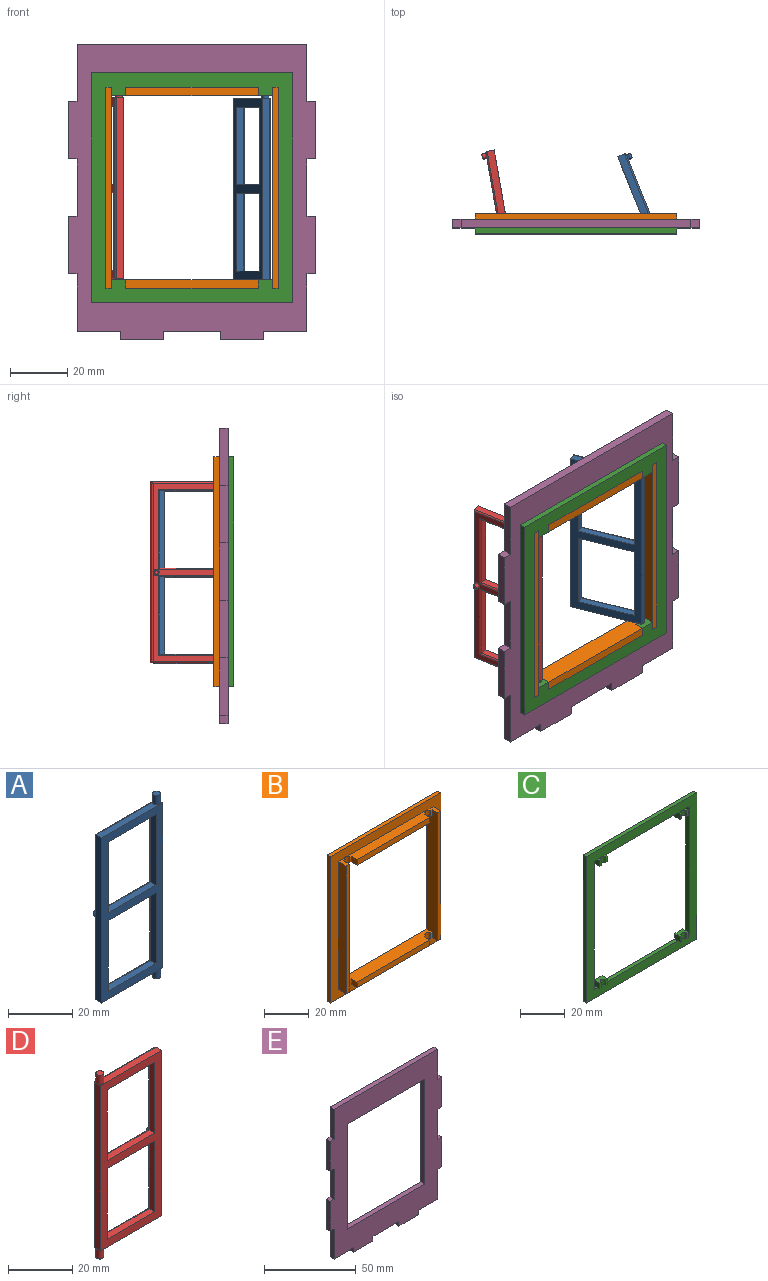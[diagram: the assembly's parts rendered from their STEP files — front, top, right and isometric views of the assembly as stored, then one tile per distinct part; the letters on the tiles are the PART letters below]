
ASSEMBLY  parts=5 mates=10
PART A: 38 faces, bbox 27x4.5x70 mm
  f0: plane 1x0.5mm, normal (0,0,-1), area 0.2mm2, adj f13,f18,f20
  f1: plane 27x2.5mm, normal (0,0,1), area 62.7mm2, adj f3,f13,f14,f17,f27
  f2: plane 27x2.5mm, normal (0,0,-1), area 62.7mm2, adj f3,f13,f14,f18,f23
  f3: plane 63x2.5mm, normal (-1,0,0), area 157.5mm2, adj f1,f2,f14,f25
  f4: plane 1x0.5mm, normal (0,0,1), area 0.2mm2, adj f13,f17,f24
  f5: plane 27x2.5mm, normal (1,0,0), area 67.5mm2, adj f6,f11,f14,f29
  f6: plane 21x2.5mm, normal (0,0,1), area 52.5mm2, adj f5,f7,f14,f28
  f7: plane 27x2.5mm, normal (-1,0,0), area 67.5mm2, adj f6,f11,f14,f30
  f8: plane 21x2.5mm, normal (0,0,-1), area 52.5mm2, adj f9,f12,f14,f33
  f9: plane 27x2.5mm, normal (1,0,0), area 67.5mm2, adj f8,f10,f14,f32
  f10: plane 21x2.5mm, normal (0,0,1), area 52.5mm2, adj f9,f12,f14,f34
  f11: plane 21x2.5mm, normal (0,0,-1), area 52.5mm2, adj f5,f7,f14,f31
  f12: plane 27x2.5mm, normal (-1,0,0), area 67.5mm2, adj f8,f10,f14,f35
  f13: plane 63x2.5mm, normal (1,0,0), area 157.5mm2, adj f0,f1,f2,f4,f14,f22
  f14: plane 63x27mm, normal (0,-1,0), area 567mm2, adj f1,f2,f3,f5,f6,f7,f8,f9
  f15: plane 62.14x26mm, normal (0,1,0), area 377mm2, adj f21,f22,f23,f25,f26,f27,f28,f29
  f16: plane 2.5x2.5mm, normal (0,0,1), area 4.9mm2, adj f17
  f17: cylinder r=1.25mm len=3.5mm, axis (0,0,-1), area 27.5mm2, adj f1,f4,f16,f26
  f18: cylinder r=1.25mm len=3.5mm, axis (0,0,-1), area 27.5mm2, adj f0,f2,f19,f21
  f19: plane 2.5x2.5mm, normal (0,0,-1), area 4.9mm2, adj f18
  f20: cylinder r=0.5mm len=0.5mm, axis (-1,0,0), area 0.2mm2, adj f0,f21,f22
  f21: bspline ~1.88x0.61mm, area 0.9mm2, adj f15,f18,f20,f23
  f22: cylinder r=0.5mm len=63mm, axis (0,0,-1), area 49.1mm2, adj f13,f15,f20,f24
  f23: cylinder r=0.5mm len=25mm, axis (-1,0,0), area 19.4mm2, adj f2,f15,f21,f25
  f24: cylinder r=0.5mm len=0.5mm, axis (1,0,0), area 0.2mm2, adj f4,f22,f26
  f25: cylinder r=0.5mm len=63mm, axis (0,0,1), area 49.1mm2, adj f3,f15,f23,f27
  f26: bspline ~1.88x0.61mm, area 0.9mm2, adj f15,f17,f24,f27
  f27: cylinder r=0.5mm len=25mm, axis (1,0,0), area 19.4mm2, adj f1,f15,f25,f26
  f28: cylinder r=0.5mm len=22mm, axis (1,0,0), area 16.9mm2, adj f6,f15,f29,f30
  f29: cylinder r=0.5mm len=28mm, axis (0,0,-1), area 21.6mm2, adj f5,f15,f28,f31
  f30: cylinder r=0.5mm len=28mm, axis (0,0,1), area 21.6mm2, adj f7,f15,f28,f31
  f31: cylinder r=0.5mm len=22mm, axis (-1,0,0), area 16.9mm2, adj f11,f15,f29,f30
  f32: cylinder r=0.5mm len=28mm, axis (0,0,-1), area 21.6mm2, adj f9,f15,f33,f34
  f33: cylinder r=0.5mm len=22mm, axis (-1,0,0), area 16.9mm2, adj f8,f15,f32,f35
  f34: cylinder r=0.5mm len=22mm, axis (1,0,0), area 16.9mm2, adj f10,f15,f32,f35
  f35: cylinder r=0.5mm len=28mm, axis (0,0,1), area 21.6mm2, adj f12,f15,f33,f34
  f36: revolved ~2x2mm, area 9.3mm2, adj f15,f37
  f37: plane 1.34x1.34mm, normal (0,1,0), area 1.4mm2, adj f36
PART B: 38 faces, bbox 70x7x80 mm
  f0: plane 56x7mm, normal (0,0,-1), area 349.9mm2, adj f10,f12,f17,f18,f30,f31,f32,f33
  f1: plane 56x7mm, normal (0,0,1), area 349.9mm2, adj f9,f12,f17,f18,f22,f23,f24,f25
  f2: plane 5x4.5mm, normal (0,0,1), area 12mm2, adj f8,f11,f17,f20,f34,f37
  f3: plane 51x5mm, normal (0,0,1), area 234mm2, adj f10,f11,f31,f32,f33,f35,f36,f37
  f4: plane 5x4.5mm, normal (0,0,1), area 12mm2, adj f11,f12,f19,f21,f30,f31
  f5: plane 5x4.5mm, normal (0,0,-1), area 12mm2, adj f8,f11,f17,f20,f26,f29
  f6: plane 5x4.5mm, normal (0,0,-1), area 12mm2, adj f11,f12,f19,f21,f24,f25
  f7: plane 51x5mm, normal (0,0,-1), area 234mm2, adj f9,f11,f22,f23,f24,f26,f27,f28
  f8: plane 70x2mm, normal (0,-1,0), area 140mm2, adj f2,f5,f17,f20
  f9: plane 46x3mm, normal (0,-1,0), area 138mm2, adj f1,f7,f22,f28
  f10: plane 46x3mm, normal (0,-1,0), area 138mm2, adj f0,f3,f33,f35
  f11: plane 80x70mm, normal (0,-1,0), area 1400mm2, adj f2,f3,f4,f5,f6,f7,f13,f14
  f12: plane 70x7mm, normal (-1,0,0), area 469mm2, adj f0,f1,f4,f6,f18,f21,f25,f30
  f13: plane 80x2mm, normal (1,0,0), area 160mm2, adj f11,f14,f16,f18
  f14: plane 70x2mm, normal (0,0,1), area 140mm2, adj f11,f13,f15,f18
  f15: plane 80x2mm, normal (-1,0,0), area 160mm2, adj f11,f14,f16,f18
  f16: plane 70x2mm, normal (0,0,-1), area 140mm2, adj f11,f13,f15,f18
  f17: plane 70x7mm, normal (1,0,0), area 469mm2, adj f0,f1,f2,f5,f8,f18,f29,f34
  f18: plane 80x70mm, normal (0,1,0), area 2016mm2, adj f0,f1,f12,f13,f14,f15,f16,f17
  f19: plane 70x5mm, normal (1,0,0), area 350mm2, adj f4,f6,f11,f21
  f20: plane 70x5mm, normal (-1,0,0), area 350mm2, adj f2,f5,f8,f11
  f21: plane 70x2mm, normal (0,-1,0), area 140mm2, adj f4,f6,f12,f19
  f22: plane 3.5x3mm, normal (1,0,0), area 10.5mm2, adj f1,f7,f9,f23
  f23: plane 3x1mm, normal (0,-1,0), area 3mm2, adj f1,f7,f22,f24
  f24: cylinder r=1.5mm len=3mm, axis (0,0,1), area 14.1mm2, adj f1,f6,f7,f23,f25
  f25: plane 3x1mm, normal (0,-1,0), area 3mm2, adj f1,f6,f12,f24
  f26: cylinder r=1.5mm len=3mm, axis (0,0,1), area 14.1mm2, adj f1,f5,f7,f27,f29
  f27: plane 3x1mm, normal (0,-1,0), area 3mm2, adj f1,f7,f26,f28
  f28: plane 3.5x3mm, normal (-1,0,0), area 10.5mm2, adj f1,f7,f9,f27
  f29: plane 3x1mm, normal (0,-1,0), area 3mm2, adj f1,f5,f17,f26
  f30: plane 3x1mm, normal (0,-1,0), area 3mm2, adj f0,f4,f12,f31
  f31: cylinder r=1.5mm len=3mm, axis (0,0,1), area 14.1mm2, adj f0,f3,f4,f30,f32
  f32: plane 3x1mm, normal (0,-1,0), area 3mm2, adj f0,f3,f31,f33
  f33: plane 3.5x3mm, normal (1,0,0), area 10.5mm2, adj f0,f3,f10,f32
  f34: plane 3x1mm, normal (0,-1,0), area 3mm2, adj f0,f2,f17,f37
  f35: plane 3.5x3mm, normal (-1,0,0), area 10.5mm2, adj f0,f3,f10,f36
  f36: plane 3x1mm, normal (0,-1,0), area 3mm2, adj f0,f3,f35,f37
  f37: cylinder r=1.5mm len=3mm, axis (0,0,1), area 14.1mm2, adj f0,f2,f3,f34,f36
PART C: 46 faces, bbox 70x3.5x80 mm
  f0: plane 5x3.5mm, normal (0,0,-1), area 14mm2, adj f4,f34,f35,f36,f37,f38
  f1: plane 5x3.5mm, normal (0,0,-1), area 14mm2, adj f4,f39,f40,f41,f42,f43
  f2: plane 5x3.5mm, normal (0,0,1), area 14mm2, adj f4,f18,f20,f26,f27,f28
  f3: plane 5x3.5mm, normal (0,0,1), area 14mm2, adj f4,f19,f21,f29,f30,f31
  f4: plane 80x70mm, normal (0,1,0), area 1460mm2, adj f0,f1,f2,f3,f12,f13,f14,f15
  f5: plane 2.5x1.5mm, normal (0,0,1), area 2mm2, adj f11,f34,f35,f36
  f6: plane 2.5x1.5mm, normal (0,0,1), area 2mm2, adj f11,f39,f40,f41
  f7: plane 2.5x1.5mm, normal (0,0,1), area 2mm2, adj f11,f41,f42,f43
  f8: plane 2.5x1.5mm, normal (0,0,-1), area 2mm2, adj f11,f20,f27,f28
  f9: plane 2.5x1.5mm, normal (0,0,-1), area 2mm2, adj f11,f18,f26,f27
  f10: plane 2.5x1.5mm, normal (0,0,-1), area 2mm2, adj f11,f19,f30,f31
  f11: plane 80x70mm, normal (0,-1,0), area 1400mm2, adj f5,f6,f7,f8,f9,f10,f12,f13
  f12: plane 80x2mm, normal (1,0,0), area 160mm2, adj f4,f11,f13,f15
  f13: plane 70x2mm, normal (0,0,1), area 140mm2, adj f4,f11,f12,f14
  f14: plane 80x2mm, normal (-1,0,0), area 160mm2, adj f4,f11,f13,f15
  f15: plane 70x2mm, normal (0,0,-1), area 140mm2, adj f4,f11,f12,f14
  f16: plane 2.5x1.5mm, normal (0,0,1), area 2mm2, adj f11,f36,f37,f38
  f17: plane 2.5x1.5mm, normal (0,0,-1), area 2mm2, adj f11,f21,f29,f30
  f18: plane 3.5x3mm, normal (1,0,0), area 10.5mm2, adj f2,f4,f9,f23,f26
  f19: plane 3.5x3mm, normal (-1,0,0), area 10.5mm2, adj f3,f4,f10,f31,f44
  f20: plane 3.5x3mm, normal (-1,0,0), area 10.5mm2, adj f2,f4,f8,f22,f28
  f21: plane 3.5x3mm, normal (1,0,0), area 10.5mm2, adj f3,f4,f17,f22,f29
  f22: plane 46x2mm, normal (0,0,1), area 92mm2, adj f4,f11,f20,f21
  f23: plane 2x2mm, normal (0,0,1), area 4mm2, adj f4,f11,f18,f33
  f24: plane 46x2mm, normal (0,0,-1), area 92mm2, adj f4,f11,f38,f39
  f25: plane 2x2mm, normal (0,0,-1), area 4mm2, adj f4,f11,f33,f34
  f26: plane 3x1mm, normal (0,-1,0), area 3mm2, adj f2,f9,f18,f27
  f27: cylinder r=1.5mm len=3mm, axis (0,0,1), area 14.1mm2, adj f2,f8,f9,f26,f28
  f28: plane 3x1mm, normal (0,-1,0), area 3mm2, adj f2,f8,f20,f27
  f29: plane 3x1mm, normal (0,-1,0), area 3mm2, adj f3,f17,f21,f30
  f30: cylinder r=1.5mm len=3mm, axis (0,0,1), area 14.1mm2, adj f3,f10,f17,f29,f31
  f31: plane 3x1mm, normal (0,-1,0), area 3mm2, adj f3,f10,f19,f30
  f32: plane 70x2mm, normal (1,0,0), area 140mm2, adj f4,f11,f44,f45
  f33: plane 70x2mm, normal (-1,0,0), area 140mm2, adj f4,f11,f23,f25
  f34: plane 3.5x3mm, normal (1,0,0), area 10.5mm2, adj f0,f4,f5,f25,f35
  f35: plane 3x1mm, normal (0,-1,0), area 3mm2, adj f0,f5,f34,f36
  f36: cylinder r=1.5mm len=3mm, axis (0,0,1), area 14.1mm2, adj f0,f5,f16,f35,f37
  f37: plane 3x1mm, normal (0,-1,0), area 3mm2, adj f0,f16,f36,f38
  f38: plane 3.5x3mm, normal (-1,0,0), area 10.5mm2, adj f0,f4,f16,f24,f37
  f39: plane 3.5x3mm, normal (1,0,0), area 10.5mm2, adj f1,f4,f6,f24,f40
  f40: plane 3x1mm, normal (0,-1,0), area 3mm2, adj f1,f6,f39,f41
  f41: cylinder r=1.5mm len=3mm, axis (0,0,1), area 14.1mm2, adj f1,f6,f7,f40,f42
  f42: plane 3x1mm, normal (0,-1,0), area 3mm2, adj f1,f7,f41,f43
  f43: plane 3.5x3mm, normal (-1,0,0), area 10.5mm2, adj f1,f4,f7,f42,f45
  f44: plane 2x2mm, normal (0,0,1), area 4mm2, adj f4,f11,f19,f32
  f45: plane 2x2mm, normal (0,0,-1), area 4mm2, adj f4,f11,f32,f43
PART D: 38 faces, bbox 27x4.5x70 mm
  f0: plane 1x0.5mm, normal (0,0,-1), area 0.2mm2, adj f13,f18,f20
  f1: plane 27x2.5mm, normal (0,0,1), area 62.7mm2, adj f3,f13,f14,f17,f27
  f2: plane 27x2.5mm, normal (0,0,-1), area 62.7mm2, adj f3,f13,f14,f18,f23
  f3: plane 63x2.5mm, normal (1,0,0), area 157.5mm2, adj f1,f2,f14,f25
  f4: plane 1x0.5mm, normal (0,0,1), area 0.2mm2, adj f13,f17,f24
  f5: plane 27x2.5mm, normal (-1,0,0), area 67.5mm2, adj f6,f11,f14,f29
  f6: plane 21x2.5mm, normal (0,0,1), area 52.5mm2, adj f5,f7,f14,f28
  f7: plane 27x2.5mm, normal (1,0,0), area 67.5mm2, adj f6,f11,f14,f30
  f8: plane 21x2.5mm, normal (0,0,-1), area 52.5mm2, adj f9,f12,f14,f33
  f9: plane 27x2.5mm, normal (-1,0,0), area 67.5mm2, adj f8,f10,f14,f32
  f10: plane 21x2.5mm, normal (0,0,1), area 52.5mm2, adj f9,f12,f14,f34
  f11: plane 21x2.5mm, normal (0,0,-1), area 52.5mm2, adj f5,f7,f14,f31
  f12: plane 27x2.5mm, normal (1,0,0), area 67.5mm2, adj f8,f10,f14,f35
  f13: plane 63x2.5mm, normal (-1,0,0), area 157.5mm2, adj f0,f1,f2,f4,f14,f22
  f14: plane 63x27mm, normal (0,-1,0), area 567mm2, adj f1,f2,f3,f5,f6,f7,f8,f9
  f15: plane 62.14x26mm, normal (0,1,0), area 377mm2, adj f21,f22,f23,f25,f26,f27,f28,f29
  f16: plane 2.5x2.5mm, normal (0,0,1), area 4.9mm2, adj f17
  f17: cylinder r=1.25mm len=3.5mm, axis (0,0,-1), area 27.5mm2, adj f1,f4,f16,f26
  f18: cylinder r=1.25mm len=3.5mm, axis (0,0,-1), area 27.5mm2, adj f0,f2,f19,f21
  f19: plane 2.5x2.5mm, normal (0,0,-1), area 4.9mm2, adj f18
  f20: cylinder r=0.5mm len=0.5mm, axis (1,0,0), area 0.2mm2, adj f0,f21,f22
  f21: bspline ~1.88x0.61mm, area 0.9mm2, adj f15,f18,f20,f23
  f22: cylinder r=0.5mm len=63mm, axis (0,0,-1), area 49.1mm2, adj f13,f15,f20,f24
  f23: cylinder r=0.5mm len=25mm, axis (1,0,0), area 19.4mm2, adj f2,f15,f21,f25
  f24: cylinder r=0.5mm len=0.5mm, axis (-1,0,0), area 0.2mm2, adj f4,f22,f26
  f25: cylinder r=0.5mm len=63mm, axis (0,0,1), area 49.1mm2, adj f3,f15,f23,f27
  f26: bspline ~1.88x0.61mm, area 0.9mm2, adj f15,f17,f24,f27
  f27: cylinder r=0.5mm len=25mm, axis (-1,0,0), area 19.4mm2, adj f1,f15,f25,f26
  f28: cylinder r=0.5mm len=22mm, axis (-1,0,0), area 16.9mm2, adj f6,f15,f29,f30
  f29: cylinder r=0.5mm len=28mm, axis (0,0,-1), area 21.6mm2, adj f5,f15,f28,f31
  f30: cylinder r=0.5mm len=28mm, axis (0,0,1), area 21.6mm2, adj f7,f15,f28,f31
  f31: cylinder r=0.5mm len=22mm, axis (1,0,0), area 16.9mm2, adj f11,f15,f29,f30
  f32: cylinder r=0.5mm len=28mm, axis (0,0,-1), area 21.6mm2, adj f9,f15,f33,f34
  f33: cylinder r=0.5mm len=22mm, axis (1,0,0), area 16.9mm2, adj f8,f15,f32,f35
  f34: cylinder r=0.5mm len=22mm, axis (-1,0,0), area 16.9mm2, adj f10,f15,f32,f35
  f35: cylinder r=0.5mm len=28mm, axis (0,0,1), area 21.6mm2, adj f12,f15,f33,f34
  f36: revolved ~2x2mm, area 9.3mm2, adj f15,f37
  f37: plane 1.34x1.34mm, normal (0,1,0), area 1.4mm2, adj f36
PART E: 34 faces, bbox 86x3x103 mm
  f0: plane 70x3mm, normal (-1,0,0), area 210mm2, adj f1,f31,f32,f33
  f1: plane 60x3mm, normal (0,0,1), area 180mm2, adj f0,f2,f32,f33
  f2: plane 70x3mm, normal (1,0,0), area 210mm2, adj f1,f31,f32,f33
  f3: plane 15x3mm, normal (0,0,-1), area 45mm2, adj f4,f30,f32,f33
  f4: plane 3x3mm, normal (-1,0,0), area 9mm2, adj f3,f5,f32,f33
  f5: plane 15x3mm, normal (0,0,-1), area 45mm2, adj f4,f6,f32,f33
  f6: plane 3x3mm, normal (1,0,0), area 9mm2, adj f5,f7,f32,f33
  f7: plane 20x3mm, normal (0,0,-1), area 60mm2, adj f6,f8,f32,f33
  f8: plane 3x3mm, normal (-1,0,0), area 9mm2, adj f7,f9,f32,f33
  f9: plane 15x3mm, normal (0,0,-1), area 45mm2, adj f8,f10,f32,f33
  f10: plane 3x3mm, normal (1,0,0), area 9mm2, adj f9,f11,f32,f33
  f11: plane 15x3mm, normal (0,0,-1), area 45mm2, adj f10,f12,f32,f33
  f12: plane 20x3mm, normal (1,0,0), area 60mm2, adj f11,f13,f32,f33
  f13: plane 3x3mm, normal (0,0,-1), area 9mm2, adj f12,f14,f32,f33
  f14: plane 20x3mm, normal (1,0,0), area 60mm2, adj f13,f15,f32,f33
  f15: plane 3x3mm, normal (0,0,1), area 9mm2, adj f14,f16,f32,f33
  f16: plane 20x3mm, normal (1,0,0), area 60mm2, adj f15,f17,f32,f33
  f17: plane 3x3mm, normal (0,0,-1), area 9mm2, adj f16,f18,f32,f33
  f18: plane 20x3mm, normal (1,0,0), area 60mm2, adj f17,f19,f32,f33
  f19: plane 3x3mm, normal (0,0,1), area 9mm2, adj f18,f20,f32,f33
  f20: plane 20x3mm, normal (1,0,0), area 60mm2, adj f19,f21,f32,f33
  f21: plane 80x3mm, normal (0,0,1), area 240mm2, adj f20,f22,f32,f33
  f22: plane 20x3mm, normal (-1,0,0), area 60mm2, adj f21,f23,f32,f33
  f23: plane 3x3mm, normal (0,0,1), area 9mm2, adj f22,f24,f32,f33
  f24: plane 20x3mm, normal (-1,0,0), area 60mm2, adj f23,f25,f32,f33
  f25: plane 3x3mm, normal (0,0,-1), area 9mm2, adj f24,f26,f32,f33
  f26: plane 20x3mm, normal (-1,0,0), area 60mm2, adj f25,f27,f32,f33
  f27: plane 3x3mm, normal (0,0,1), area 9mm2, adj f26,f28,f32,f33
  f28: plane 20x3mm, normal (-1,0,0), area 60mm2, adj f27,f29,f32,f33
  f29: plane 3x3mm, normal (0,0,-1), area 9mm2, adj f28,f30,f32,f33
  f30: plane 20x3mm, normal (-1,0,0), area 60mm2, adj f3,f29,f32,f33
  f31: plane 60x3mm, normal (0,0,-1), area 180mm2, adj f0,f2,f32,f33
  f32: plane 103x86mm, normal (0,-1,0), area 4130mm2, adj f0,f1,f2,f3,f4,f5,f6,f7
  f33: plane 103x86mm, normal (0,1,0), area 4130mm2, adj f0,f1,f2,f3,f4,f5,f6,f7
PLACE A rot(axis=(0,0,-1),68.1deg) t=(-28.46,18.34,7.94)mm
PLACE B t=(-39.34,-14.58,8.44)mm
PLACE C rot(axis=(1,0,0),180deg) t=(-39.34,-21.58,8.44)mm
PLACE D rot(axis=(0,0,1),99.9deg) t=(-66.94,-6.01,8.19)mm
PLACE E t=(-39.34,-16.58,8.44)mm fixed
MATE revolute D.f17 <-> C.f30  axis (0,0,-1) through (-64.84,-18.08,-25.06)mm
MATE planar B.f20 <-> E.f2  axis (-1,0,0) through (-69.34,-19.08,8.44)mm
MATE planar B.f3 <-> E.f31  axis (0,0,1) through (-39.34,-19.05,43.44)mm
MATE planar B.f11 <-> E.f33  axis (0,-1,0) through (-9.34,-16.58,43.44)mm
MATE planar C.f16 <-> E.f1  axis (0,0,-1) through (-15.63,-18.93,-26.56)mm
MATE planar C.f11 <-> E.f32  axis (0,1,0) through (-62.34,-19.58,-26.56)mm
MATE planar C.f32 <-> B.f20  axis (1,0,0) through (-69.34,-20.58,8.44)mm
MATE planar A.f2 <-> B.f1  axis (0,0,-1) through (-19,-5.94,-23.56)mm
MATE cylindrical A.f17 <-> C.f27  axis (0,0,-1) through (-13.84,-18.08,-25.31)mm
MATE planar D.f2 <-> B.f1  axis (0,0,-1) through (-66.84,-5.04,-23.31)mm
